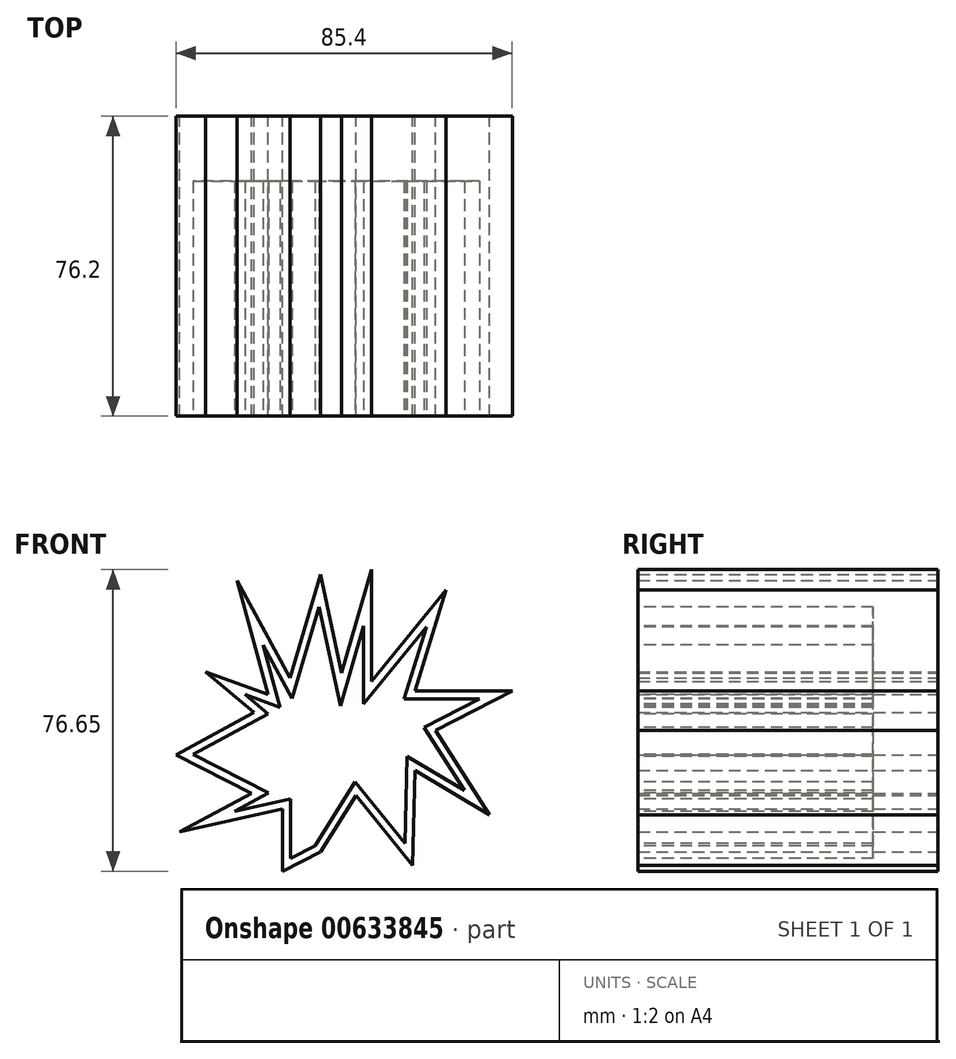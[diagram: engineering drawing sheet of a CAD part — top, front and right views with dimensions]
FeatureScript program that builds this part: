
annotation { "Feature Type Name" : "Feature", "Feature Type Description" : "" }
export const myFeature = defineFeature(function(context is Context, id is Id, definition is map)
    precondition{}
    {
        {
            var Q0;
            Q0=qCreatedBy(makeId("Front.planeOp"),FACE);
            var sketch = newSketch(context, id + "F0", { "sketchPlane" : qUnion([Q0])});
            skLineSegment(sketch, "E0", {"start": v(0, -26.72) * mm, "end": v(9, -12.37) * mm});
            skLineSegment(sketch, "E1", {"start": v(9, -12.37) * mm, "end": v(23.36, -30.08) * mm});
            skLineSegment(sketch, "E2", {"start": v(23.36, -30.08) * mm, "end": v(23.97, -5.95) * mm});
            skLineSegment(sketch, "E3", {"start": v(23.97, -5.95) * mm, "end": v(42.9, -17.25) * mm});
            skLineSegment(sketch, "E4", {"start": v(42.9, -17.25) * mm, "end": v(29.16, 4.12) * mm});
            skLineSegment(sketch, "E5", {"start": v(29.16, 4.12) * mm, "end": v(48.7, 14.2) * mm});
            skLineSegment(sketch, "E6", {"start": v(48.7, 14.2) * mm, "end": v(23.97, 14.2) * mm});
            skLineSegment(sketch, "E7", {"start": v(23.97, 14.2) * mm, "end": v(31.9, 39.85) * mm});
            skLineSegment(sketch, "E8", {"start": v(31.9, 39.85) * mm, "end": v(12.98, 16.64) * mm});
            skLineSegment(sketch, "E9", {"start": v(12.98, 16.64) * mm, "end": v(12.98, 45.04) * mm});
            skLineSegment(sketch, "E10", {"start": v(12.98, 45.04) * mm, "end": v(5.34, 18.78) * mm});
            skLineSegment(sketch, "E11", {"start": v(5.34, 18.78) * mm, "end": v(0, 43.82) * mm});
            skLineSegment(sketch, "E12", {"start": v(0, 43.82) * mm, "end": v(-7.8, 17.56) * mm});
            skLineSegment(sketch, "E13", {"start": v(-7.8, 17.56) * mm, "end": v(-21.23, 42.3) * mm});
            skLineSegment(sketch, "E14", {"start": v(-21.23, 42.3) * mm, "end": v(-13.29, 13.28) * mm});
            skLineSegment(sketch, "E15", {"start": v(-13.29, 13.28) * mm, "end": v(-29.17, 19.09) * mm});
            skLineSegment(sketch, "E16", {"start": v(-29.17, 19.09) * mm, "end": v(-16.95, 8.7) * mm});
            skLineSegment(sketch, "E17", {"start": v(-16.95, 8.7) * mm, "end": v(-36.7, -2.02) * mm});
            skLineSegment(sketch, "E18", {"start": v(-36.7, -2.02) * mm, "end": v(-17.56, -11.76) * mm});
            skLineSegment(sketch, "E19", {"start": v(-17.56, -11.76) * mm, "end": v(-35.79, -21.66) * mm});
            skLineSegment(sketch, "E20", {"start": v(-35.79, -21.66) * mm, "end": v(-9.62, -15.73) * mm});
            skLineSegment(sketch, "E21", {"start": v(-9.62, -15.73) * mm, "end": v(-9.62, -31.6) * mm});
            skLineSegment(sketch, "E22", {"start": v(-9.62, -31.6) * mm, "end": v(0, -26.72) * mm});
            skSolve(sketch);
        }
        {
            var Q0;
            Q0=makeQuery(id+"F0.imprint","IMPRINT",FACE,{"disambiguationData":[TD([[makeQuery(id+"F0.imprint","IMPRINT",EDGE,{"derivedFrom":sQuery(id+"F0.wireOp",EDGE,"E0")}),1.0]])]});
            extrude(context, id + "F1", {"entities" : qUnion([Q0]), "depth" : 76.2 * mm, "offsetDistance" : 25.4 * mm});
        }
        {
            var Q0;
            Q0=makeQuery(id+"F1.opExtrude","CAP_FACE",FACE,{"disambiguationData":[OSD([sQuery(id+"F0.wireOp",EDGE,"E0"),sQuery(id+"F0.wireOp",EDGE,"E1"),sQuery(id+"F0.wireOp",EDGE,"E2"),sQuery(id+"F0.wireOp",EDGE,"E3"),sQuery(id+"F0.wireOp",EDGE,"E4"),sQuery(id+"F0.wireOp",EDGE,"E5"),sQuery(id+"F0.wireOp",EDGE,"E6"),sQuery(id+"F0.wireOp",EDGE,"E7"),sQuery(id+"F0.wireOp",EDGE,"E8"),sQuery(id+"F0.wireOp",EDGE,"E9"),sQuery(id+"F0.wireOp",EDGE,"E10"),sQuery(id+"F0.wireOp",EDGE,"E11"),sQuery(id+"F0.wireOp",EDGE,"E12"),sQuery(id+"F0.wireOp",EDGE,"E13"),sQuery(id+"F0.wireOp",EDGE,"E14"),sQuery(id+"F0.wireOp",EDGE,"E15"),sQuery(id+"F0.wireOp",EDGE,"E16"),sQuery(id+"F0.wireOp",EDGE,"E17"),sQuery(id+"F0.wireOp",EDGE,"E18"),sQuery(id+"F0.wireOp",EDGE,"E19"),sQuery(id+"F0.wireOp",EDGE,"E20"),sQuery(id+"F0.wireOp",EDGE,"E21"),sQuery(id+"F0.wireOp",EDGE,"E22")])],"isStart":false});
            var sketch = newSketch(context, id + "F2", { "sketchPlane" : qUnion([Q0])});
            skLineSegment(sketch, "E23.0", {"start": v(26.88, 30.47) * mm, "end": v(10.94, 10.94) * mm});
            skLineSegment(sketch, "E23.1", {"start": v(21.21, 12.17) * mm, "end": v(26.88, 30.47) * mm});
            skLineSegment(sketch, "E23.2", {"start": v(40.33, 12.17) * mm, "end": v(21.21, 12.17) * mm});
            skLineSegment(sketch, "E23.3", {"start": v(26.24, 4.9) * mm, "end": v(40.33, 12.17) * mm});
            skLineSegment(sketch, "E23.4", {"start": v(36.52, -11.08) * mm, "end": v(26.24, 4.9) * mm});
            skLineSegment(sketch, "E23.5", {"start": v(22.03, -2.43) * mm, "end": v(36.52, -11.08) * mm});
            skLineSegment(sketch, "E23.6", {"start": v(-7.6, -28.3) * mm, "end": v(-1.42, -25.16) * mm});
            skLineSegment(sketch, "E23.7", {"start": v(-1.42, -25.16) * mm, "end": v(8.8, -8.88) * mm});
            skLineSegment(sketch, "E23.8", {"start": v(8.8, -8.88) * mm, "end": v(21.47, -24.52) * mm});
            skLineSegment(sketch, "E23.9", {"start": v(21.47, -24.52) * mm, "end": v(22.03, -2.43) * mm});
            skLineSegment(sketch, "E23.10", {"start": v(-7.6, -13.18) * mm, "end": v(-7.6, -28.3) * mm});
            skLineSegment(sketch, "E23.11", {"start": v(10.94, 10.94) * mm, "end": v(10.94, 30.77) * mm});
            skLineSegment(sketch, "E23.12", {"start": v(10.94, 30.77) * mm, "end": v(5.04, 10.46) * mm});
            skLineSegment(sketch, "E23.13", {"start": v(5.04, 10.46) * mm, "end": v(-0.32, 35.6) * mm});
            skLineSegment(sketch, "E23.14", {"start": v(-0.32, 35.6) * mm, "end": v(-7.24, 12.28) * mm});
            skLineSegment(sketch, "E23.15", {"start": v(-7.24, 12.28) * mm, "end": v(-14.63, 25.9) * mm});
            skLineSegment(sketch, "E23.16", {"start": v(-14.63, 25.9) * mm, "end": v(-10.29, 10.03) * mm});
            skLineSegment(sketch, "E23.17", {"start": v(-10.29, 10.03) * mm, "end": v(-19.2, 13.28) * mm});
            skLineSegment(sketch, "E23.18", {"start": v(-19.2, 13.28) * mm, "end": v(-13.38, 8.33) * mm});
            skLineSegment(sketch, "E23.19", {"start": v(-13.38, 8.33) * mm, "end": v(-32.34, -1.97) * mm});
            skLineSegment(sketch, "E23.20", {"start": v(-32.34, -1.97) * mm, "end": v(-13.2, -11.7) * mm});
            skLineSegment(sketch, "E23.21", {"start": v(-13.2, -11.7) * mm, "end": v(-21.9, -16.43) * mm});
            skLineSegment(sketch, "E23.22", {"start": v(-21.9, -16.43) * mm, "end": v(-7.6, -13.18) * mm});
            skSolve(sketch);
        }
        {
            var Q0;
            Q0=makeQuery(id+"F2.imprint","IMPRINT",FACE,{"disambiguationData":[TD([[makeQuery(id+"F2.imprint","IMPRINT",EDGE,{"derivedFrom":sQuery(id+"F2.wireOp",EDGE,"E23.0")}),1.0]])]});
            extrude(context, id + "F3", {"entities" : qUnion([Q0]), "operationType" : NewBodyOperationType.REMOVE, "oppositeDirection" : true, "depth" : 59.69 * mm, "offsetDistance" : 25.4 * mm});
        }
    });
